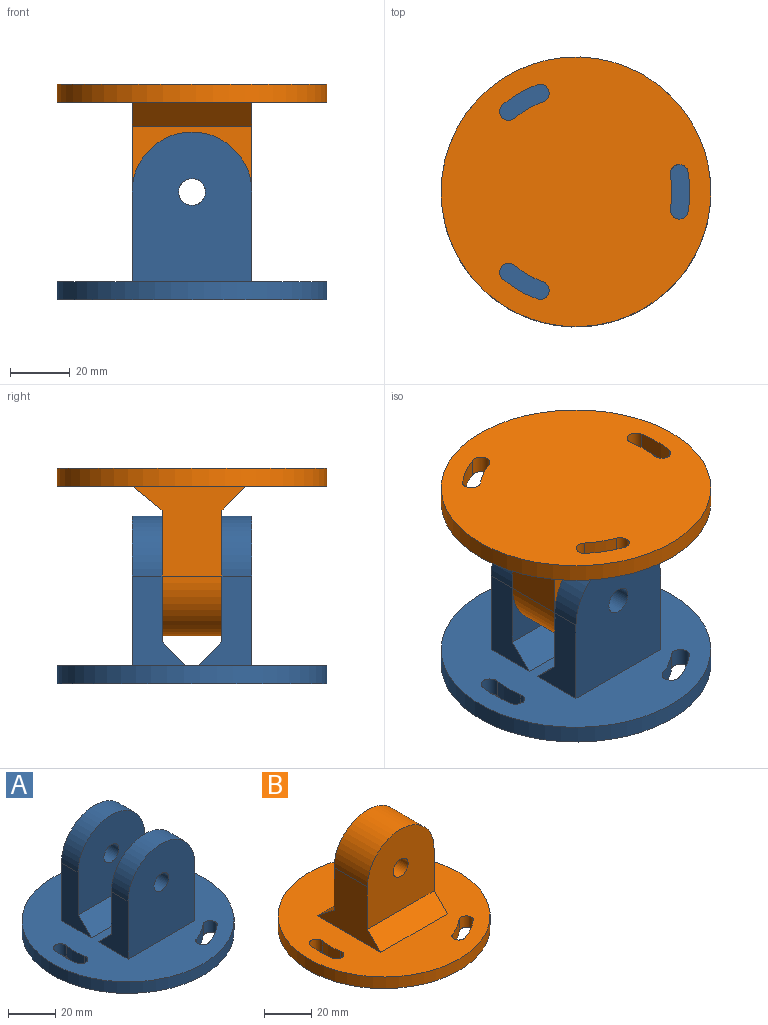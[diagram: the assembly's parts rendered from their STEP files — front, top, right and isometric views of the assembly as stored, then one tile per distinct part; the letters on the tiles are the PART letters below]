
ASSEMBLY  parts=2 mates=1
PART A: 29 faces, bbox 90x90x56 mm
  f0: plane 90x90mm, normal (0,0,1), area 4617mm2, adj f3,f4,f5,f6,f7,f8,f9,f10
  f1: plane 42x40mm, normal (0,-1,0), area 1444.7mm2, adj f21,f22,f25,f26,f27
  f2: plane 42x40mm, normal (0,1,0), area 1444.7mm2, adj f4,f6,f23,f24,f28
  f3: plane 50x40mm, normal (0,-1,0), area 1764.7mm2, adj f0,f4,f6,f23,f24
  f4: plane 30x18mm, normal (-1,0,0), area 332mm2, adj f0,f2,f3,f24,f28
  f5: plane 50x40mm, normal (0,1,0), area 1764.7mm2, adj f0,f21,f22,f25,f26
  f6: plane 30x18mm, normal (1,0,0), area 332mm2, adj f0,f2,f3,f24,f28
  f7: cylinder r=3mm len=6mm, axis (0,0,-1), area 56.5mm2, adj f0,f8,f19,f20
  f8: cylinder r=32mm len=9.62mm, axis (0,0,-1), area 67mm2, adj f0,f7,f9,f20
  f9: cylinder r=3mm len=6mm, axis (0,0,-1), area 56.5mm2, adj f0,f8,f19,f20
  f10: cylinder r=3mm len=6mm, axis (0,0,-1), area 56.5mm2, adj f0,f11,f17,f20
  f11: cylinder r=32mm len=11.11mm, axis (0,0,-1), area 67mm2, adj f0,f10,f12,f20
  f12: cylinder r=3mm len=6mm, axis (0,0,-1), area 56.5mm2, adj f0,f11,f17,f20
  f13: cylinder r=32mm len=9.62mm, axis (0,0,-1), area 67mm2, adj f0,f14,f18,f20
  f14: cylinder r=3mm len=6mm, axis (0,0,-1), area 56.5mm2, adj f0,f13,f15,f20
  f15: cylinder r=38mm len=11.43mm, axis (0,0,-1), area 79.6mm2, adj f0,f14,f18,f20
  f16: cylinder r=45mm len=90mm, axis (0,0,-1), area 1696.5mm2, adj f0,f20
  f17: cylinder r=38mm len=13.2mm, axis (0,0,-1), area 79.6mm2, adj f0,f10,f12,f20
  f18: cylinder r=3mm len=6mm, axis (0,0,-1), area 56.5mm2, adj f0,f13,f15,f20
  f19: cylinder r=38mm len=11.43mm, axis (0,0,-1), area 79.6mm2, adj f0,f7,f9,f20
  f20: plane 90x90mm, normal (0,0,-1), area 6057mm2, adj f7,f8,f9,f10,f11,f12,f13,f14
  f21: plane 30x18mm, normal (-1,0,0), area 332mm2, adj f0,f1,f5,f26,f27
  f22: plane 30x18mm, normal (1,0,0), area 332mm2, adj f0,f1,f5,f26,f27
  f23: cylinder r=4.5mm len=10mm, axis (0,-1,0), area 282.7mm2, adj f2,f3
  f24: cylinder r=20mm len=40mm, axis (0,-1,0), area 628.3mm2, adj f2,f3,f4,f6
  f25: cylinder r=4.5mm len=10mm, axis (0,-1,0), area 282.7mm2, adj f1,f5
  f26: cylinder r=20mm len=40mm, axis (0,-1,0), area 628.3mm2, adj f1,f5,f21,f22
  f27: plane 40x8mm, normal (0,-0.71,0.71), area 452.5mm2, adj f0,f1,f21,f22
  f28: plane 40x8mm, normal (0,0.71,0.71), area 452.5mm2, adj f0,f2,f4,f6
PART B: 23 faces, bbox 90x90x56 mm
  f0: plane 42x40mm, normal (0,1,0), area 1444.7mm2, adj f1,f2,f19,f21,f22
  f1: plane 38x30mm, normal (-1,0,0), area 672mm2, adj f0,f3,f17,f19,f20,f21
  f2: plane 38x30mm, normal (1,0,0), area 672mm2, adj f0,f3,f17,f19,f20,f21
  f3: plane 42x40mm, normal (0,-1,0), area 1444.7mm2, adj f1,f2,f20,f21,f22
  f4: cylinder r=3mm len=6mm, axis (0,0,-1), area 56.5mm2, adj f5,f16,f17,f18
  f5: cylinder r=38mm len=13.2mm, axis (0,0,-1), area 79.6mm2, adj f4,f6,f17,f18
  f6: cylinder r=3mm len=6mm, axis (0,0,-1), area 56.5mm2, adj f5,f16,f17,f18
  f7: cylinder r=3mm len=6mm, axis (0,0,-1), area 56.5mm2, adj f8,f13,f17,f18
  f8: cylinder r=38mm len=11.43mm, axis (0,0,-1), area 79.6mm2, adj f7,f9,f17,f18
  f9: cylinder r=3mm len=6mm, axis (0,0,-1), area 56.5mm2, adj f8,f13,f17,f18
  f10: cylinder r=38mm len=11.43mm, axis (0,0,-1), area 79.6mm2, adj f11,f14,f17,f18
  f11: cylinder r=3mm len=6mm, axis (0,0,-1), area 56.5mm2, adj f10,f12,f17,f18
  f12: cylinder r=32mm len=9.62mm, axis (0,0,-1), area 67mm2, adj f11,f14,f17,f18
  f13: cylinder r=32mm len=9.62mm, axis (0,0,-1), area 67mm2, adj f7,f9,f17,f18
  f14: cylinder r=3mm len=6mm, axis (0,0,-1), area 56.5mm2, adj f10,f12,f17,f18
  f15: cylinder r=45mm len=90mm, axis (0,0,-1), area 1696.5mm2, adj f17,f18
  f16: cylinder r=32mm len=11.11mm, axis (0,0,-1), area 67mm2, adj f4,f6,f17,f18
  f17: plane 90x90mm, normal (0,0,1), area 4537mm2, adj f1,f2,f4,f5,f6,f7,f8,f9
  f18: plane 90x90mm, normal (0,0,-1), area 6057mm2, adj f4,f5,f6,f7,f8,f9,f10,f11
  f19: plane 40x10mm, normal (0,0.62,0.78), area 512.2mm2, adj f0,f1,f2,f17
  f20: plane 40x8mm, normal (0,-0.71,0.71), area 452.5mm2, adj f1,f2,f3,f17
  f21: cylinder r=20mm len=40mm, axis (0,-1,0), area 1256.6mm2, adj f0,f1,f2,f3
  f22: cylinder r=4.5mm len=20mm, axis (0,-1,0), area 565.5mm2, adj f0,f3
PLACE A t=(-28.97,1.69,-16.38)mm
PLACE B rot(axis=(0,-1,0),180deg) t=(-28.97,1.69,55.62)mm
MATE pin_slot B.f21 <-> A.f23  axis (0,-1,0) through (-28.97,-8.31,19.62)mm
